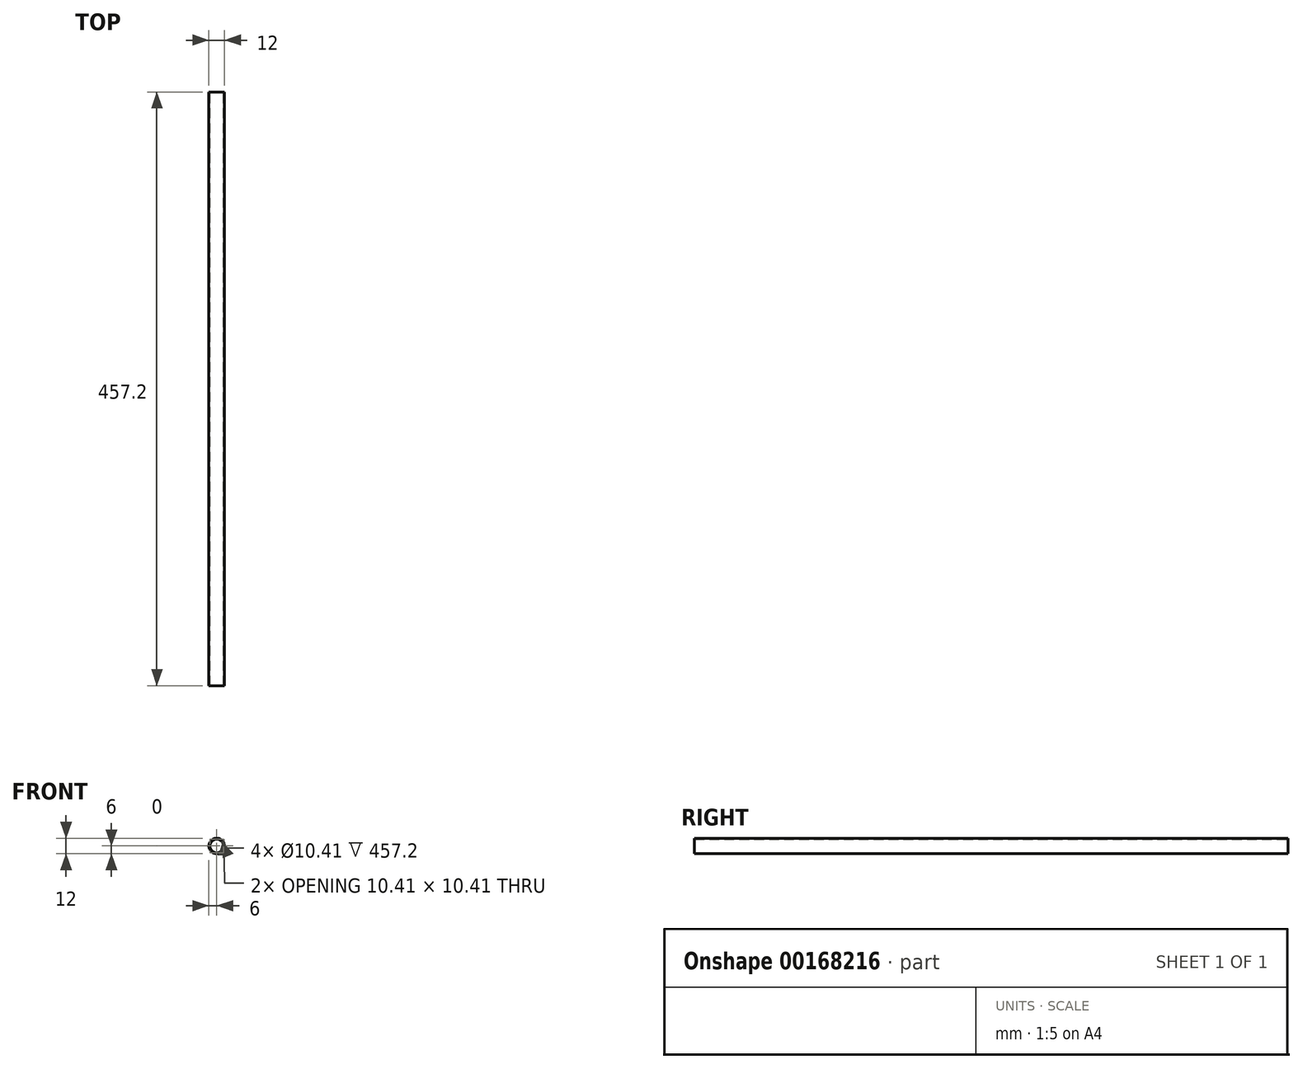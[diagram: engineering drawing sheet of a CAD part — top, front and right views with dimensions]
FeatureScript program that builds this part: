
annotation { "Feature Type Name" : "Feature", "Feature Type Description" : "" }
export const myFeature = defineFeature(function(context is Context, id is Id, definition is map)
    precondition{}
    {
        {
            var Q0;
            Q0=qCreatedBy(makeId("Front.planeOp"),FACE);
            var sketch = newSketch(context, id + "F0", { "sketchPlane" : qUnion([Q0])});
            skCircle(sketch, "E0", {"center": v(0, 0) * mm, "radius": 6 * mm});
            skSolve(sketch);
        }
        {
            var Q0;
            Q0 = qSketchRegion(id + "F0", true);
            extrude(context, id + "F1", {"entities" : qUnion([Q0]), "depth" : 457.2 * mm, "offsetDistance" : 25 * mm});
        }
        {
            var Q0;
            Q0=makeQuery(id+"F1.opExtrude","CAP_FACE",FACE,{"disambiguationData":[OSD([sQuery(id+"F0.wireOp",EDGE,"E0")])],"isStart":true});
            var sketch = newSketch(context, id + "F2", { "sketchPlane" : qUnion([Q0])});
            skCircle(sketch, "E1", {"center": v(0, 0) * mm, "radius": 5.2 * mm});
            skSolve(sketch);
        }
        {
            var Q0;
            Q0 = qSketchRegion(id + "F2", true);
            extrude(context, id + "F3", {"entities" : qUnion([Q0]), "operationType" : NewBodyOperationType.REMOVE, "endBound" : BoundingType.THROUGH_ALL, "oppositeDirection" : true, "depth" : 25 * mm, "offsetDistance" : 25 * mm});
        }
    });
